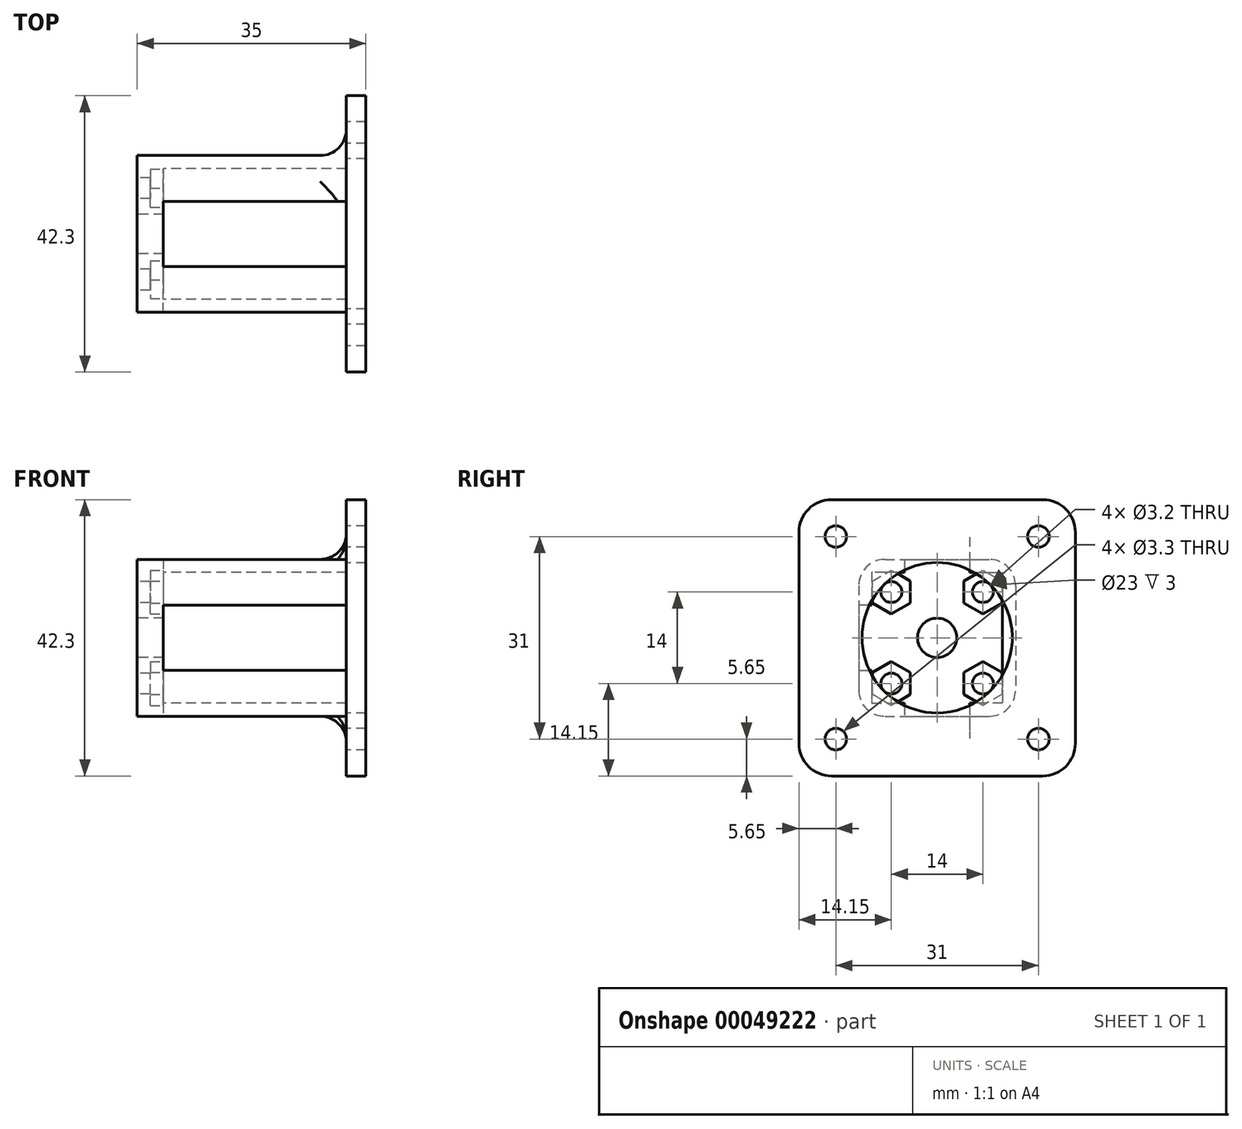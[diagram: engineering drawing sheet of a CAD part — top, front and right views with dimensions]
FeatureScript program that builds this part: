
annotation { "Feature Type Name" : "Feature", "Feature Type Description" : "" }
export const myFeature = defineFeature(function(context is Context, id is Id, definition is map)
    precondition{}
    {
        {
            var Q0;
            Q0=qCreatedBy(makeId("Right.planeOp"),FACE);
            var sketch = newSketch(context, id + "F0", { "sketchPlane" : qUnion([Q0])});
            skCircle(sketch, "E0", {"center": v(-15.5, 15.5) * mm, "radius": 1.65 * mm});
            skCircle(sketch, "E1", {"center": v(-15.5, -15.5) * mm, "radius": 1.65 * mm});
            skCircle(sketch, "E2", {"center": v(15.5, -15.5) * mm, "radius": 1.65 * mm});
            skCircle(sketch, "E3", {"center": v(15.5, 15.5) * mm, "radius": 1.65 * mm});
            skLineSegment(sketch, "E4", {"start": v(0, 0) * mm, "end": v(-15.5, 15.5) * mm, "construction": true});
            skLineSegment(sketch, "E5", {"start": v(0, 0) * mm, "end": v(15.5, -15.5) * mm, "construction": true});
            skLineSegment(sketch, "E6", {"start": v(15.5, 15.5) * mm, "end": v(0, 0) * mm, "construction": true});
            skLineSegment(sketch, "E7", {"start": v(0, 0) * mm, "end": v(-15.5, -15.5) * mm, "construction": true});
            skLineSegment(sketch, "E8.bottom", {"start": v(-21.15, 21.15) * mm, "end": v(21.15, 21.15) * mm, "construction": true});
            skLineSegment(sketch, "E8.top", {"start": v(-21.15, -21.15) * mm, "end": v(21.15, -21.15) * mm, "construction": true});
            skLineSegment(sketch, "E8.left", {"start": v(-21.15, 21.15) * mm, "end": v(-21.15, -21.15) * mm, "construction": true});
            skLineSegment(sketch, "E8.right", {"start": v(21.15, 21.15) * mm, "end": v(21.15, -21.15) * mm, "construction": true});
            skPoint(sketch, "E8.middle", {"position": v(0, 0) * mm});
            skCircle(sketch, "E9", {"center": v(-7, 7) * mm, "radius": 1.6 * mm});
            skCircle(sketch, "E10", {"center": v(-7, -7) * mm, "radius": 1.6 * mm});
            skCircle(sketch, "E11", {"center": v(7, -7) * mm, "radius": 1.6 * mm});
            skCircle(sketch, "E12", {"center": v(7, 7) * mm, "radius": 1.6 * mm});
            skLineSegment(sketch, "E13", {"start": v(-7, 7) * mm, "end": v(7, -7) * mm, "construction": true});
            skLineSegment(sketch, "E14", {"start": v(7, 7) * mm, "end": v(-7, -7) * mm, "construction": true});
            skLineSegment(sketch, "E15.bottom", {"start": v(-7, 7) * mm, "end": v(7, 7) * mm, "construction": true});
            skLineSegment(sketch, "E15.top", {"start": v(-7, -7) * mm, "end": v(7, -7) * mm, "construction": true});
            skLineSegment(sketch, "E15.left", {"start": v(-7, 7) * mm, "end": v(-7, -7) * mm, "construction": true});
            skLineSegment(sketch, "E15.right", {"start": v(7, 7) * mm, "end": v(7, -7) * mm, "construction": true});
            skLineSegment(sketch, "E16.bottom", {"start": v(-12, 12) * mm, "end": v(12, 12) * mm});
            skLineSegment(sketch, "E16.top", {"start": v(-12, -12) * mm, "end": v(12, -12) * mm});
            skLineSegment(sketch, "E16.left", {"start": v(-12, 12) * mm, "end": v(-12, -12) * mm});
            skLineSegment(sketch, "E16.right", {"start": v(12, 12) * mm, "end": v(12, -12) * mm});
            skCircle(sketch, "E17", {"center": v(0, 0) * mm, "radius": 3 * mm});
            skSolve(sketch);
        }
        {
            var Q0;
            Q0=makeQuery(id+"F0.imprint","IMPRINT",FACE,{"disambiguationData":[TD([[makeQuery(id+"F0.imprint","IMPRINT",EDGE,{"derivedFrom":sQuery(id+"F0.wireOp",EDGE,"E9")}),-1.0]])]});
            extrude(context, id + "F1", {"entities" : qUnion([Q0]), "depth" : 4 * mm, "offsetDistance" : 25 * mm});
        }
        {
            var Q0;
            Q0=makeQuery(id+"F1.opExtrude","CAP_FACE",FACE,{"disambiguationData":[OSD([sQuery(id+"F0.wireOp",EDGE,"E9"),sQuery(id+"F0.wireOp",EDGE,"E10"),sQuery(id+"F0.wireOp",EDGE,"E11"),sQuery(id+"F0.wireOp",EDGE,"E12"),sQuery(id+"F0.wireOp",EDGE,"E16.bottom"),sQuery(id+"F0.wireOp",EDGE,"E16.top"),sQuery(id+"F0.wireOp",EDGE,"E16.left"),sQuery(id+"F0.wireOp",EDGE,"E16.right"),sQuery(id+"F0.wireOp",EDGE,"E17")])],"isStart":false});
            var sketch = newSketch(context, id + "F2", { "sketchPlane" : qUnion([Q0])});
            skCircle(sketch, "E18.cCircle", {"center": v(7, -7) * mm, "radius": 2.9 * mm, "construction": true});
            skLineSegment(sketch, "E18.0", {"start": v(4.1, -5.33) * mm, "end": v(7, -3.65) * mm});
            skLineSegment(sketch, "E18.1", {"start": v(7, -3.65) * mm, "end": v(9.9, -5.33) * mm});
            skLineSegment(sketch, "E18.2", {"start": v(9.9, -5.33) * mm, "end": v(9.9, -8.67) * mm});
            skLineSegment(sketch, "E18.3", {"start": v(9.9, -8.67) * mm, "end": v(7, -10.35) * mm});
            skLineSegment(sketch, "E18.4", {"start": v(7, -10.35) * mm, "end": v(4.1, -8.67) * mm});
            skLineSegment(sketch, "E18.5", {"start": v(4.1, -8.67) * mm, "end": v(4.1, -5.33) * mm});
            skPoint(sketch, "E18.0.midPoint", {"position": v(5.55, -4.49) * mm});
            skCircle(sketch, "E19.cCircle", {"center": v(7, 7) * mm, "radius": 2.9 * mm, "construction": true});
            skLineSegment(sketch, "E19.0", {"start": v(7, 3.65) * mm, "end": v(4.1, 5.33) * mm});
            skLineSegment(sketch, "E19.1", {"start": v(4.1, 5.33) * mm, "end": v(4.1, 8.67) * mm});
            skLineSegment(sketch, "E19.2", {"start": v(4.1, 8.67) * mm, "end": v(7, 10.35) * mm});
            skLineSegment(sketch, "E19.3", {"start": v(7, 10.35) * mm, "end": v(9.9, 8.67) * mm});
            skLineSegment(sketch, "E19.4", {"start": v(9.9, 8.67) * mm, "end": v(9.9, 5.33) * mm});
            skLineSegment(sketch, "E19.5", {"start": v(9.9, 5.33) * mm, "end": v(7, 3.65) * mm});
            skPoint(sketch, "E19.0.midPoint", {"position": v(5.55, 4.49) * mm});
            skCircle(sketch, "E20.cCircle", {"center": v(-7, 7) * mm, "radius": 2.9 * mm, "construction": true});
            skLineSegment(sketch, "E20.0", {"start": v(-7, 3.65) * mm, "end": v(-9.9, 5.33) * mm});
            skLineSegment(sketch, "E20.1", {"start": v(-9.9, 5.33) * mm, "end": v(-9.9, 8.67) * mm});
            skLineSegment(sketch, "E20.2", {"start": v(-9.9, 8.67) * mm, "end": v(-7, 10.35) * mm});
            skLineSegment(sketch, "E20.3", {"start": v(-7, 10.35) * mm, "end": v(-4.1, 8.67) * mm});
            skLineSegment(sketch, "E20.4", {"start": v(-4.1, 8.67) * mm, "end": v(-4.1, 5.33) * mm});
            skLineSegment(sketch, "E20.5", {"start": v(-4.1, 5.33) * mm, "end": v(-7, 3.65) * mm});
            skPoint(sketch, "E20.0.midPoint", {"position": v(-8.45, 4.49) * mm});
            skCircle(sketch, "E21.cCircle", {"center": v(-7, -7) * mm, "radius": 2.9 * mm, "construction": true});
            skLineSegment(sketch, "E21.0", {"start": v(-7, -3.65) * mm, "end": v(-4.1, -5.33) * mm});
            skLineSegment(sketch, "E21.1", {"start": v(-4.1, -5.33) * mm, "end": v(-4.1, -8.67) * mm});
            skLineSegment(sketch, "E21.2", {"start": v(-4.1, -8.67) * mm, "end": v(-7, -10.35) * mm});
            skLineSegment(sketch, "E21.3", {"start": v(-7, -10.35) * mm, "end": v(-9.9, -8.67) * mm});
            skLineSegment(sketch, "E21.4", {"start": v(-9.9, -8.67) * mm, "end": v(-9.9, -5.33) * mm});
            skLineSegment(sketch, "E21.5", {"start": v(-9.9, -5.33) * mm, "end": v(-7, -3.65) * mm});
            skPoint(sketch, "E21.0.midPoint", {"position": v(-5.55, -4.49) * mm});
            skSolve(sketch);
        }
        {
            var Q0;
            Q0=makeQuery(id+"F1.opExtrude","CAP_FACE",FACE,{"disambiguationData":[OSD([sQuery(id+"F0.wireOp",EDGE,"E9"),sQuery(id+"F0.wireOp",EDGE,"E10"),sQuery(id+"F0.wireOp",EDGE,"E11"),sQuery(id+"F0.wireOp",EDGE,"E12"),sQuery(id+"F0.wireOp",EDGE,"E16.bottom"),sQuery(id+"F0.wireOp",EDGE,"E16.top"),sQuery(id+"F0.wireOp",EDGE,"E16.left"),sQuery(id+"F0.wireOp",EDGE,"E16.right"),sQuery(id+"F0.wireOp",EDGE,"E17")])],"isStart":false});
            var sketch = newSketch(context, id + "F3", { "sketchPlane" : qUnion([Q0])});
            skLineSegment(sketch, "E22.bottom", {"start": v(-12, 12) * mm, "end": v(12, 12) * mm});
            skLineSegment(sketch, "E22.top", {"start": v(-12, -12) * mm, "end": v(12, -12) * mm});
            skLineSegment(sketch, "E22.left", {"start": v(-12, 12) * mm, "end": v(-12, -12) * mm});
            skLineSegment(sketch, "E22.right", {"start": v(12, 12) * mm, "end": v(12, -12) * mm});
            skLineSegment(sketch, "E23", {"start": v(-10, 10) * mm, "end": v(-10, 5) * mm});
            skLineSegment(sketch, "E24", {"start": v(-10, 5) * mm, "end": v(-12, 5) * mm});
            skLineSegment(sketch, "E25", {"start": v(-12, 5) * mm, "end": v(-12, 12) * mm});
            skLineSegment(sketch, "E26", {"start": v(-5, 12) * mm, "end": v(-5, 10) * mm});
            skLineSegment(sketch, "E27", {"start": v(-5, 10) * mm, "end": v(-10, 10) * mm});
            skLineSegment(sketch, "E28", {"start": v(-10, -5) * mm, "end": v(-10, -10) * mm});
            skLineSegment(sketch, "E29", {"start": v(-10, -10) * mm, "end": v(-5, -10) * mm});
            skLineSegment(sketch, "E30", {"start": v(-5, -10) * mm, "end": v(-5, -12) * mm});
            skLineSegment(sketch, "E31", {"start": v(-5, -12) * mm, "end": v(-12, -12) * mm});
            skLineSegment(sketch, "E32", {"start": v(-12, -12) * mm, "end": v(-12, -5) * mm});
            skLineSegment(sketch, "E33", {"start": v(-12, -5) * mm, "end": v(-10, -5) * mm});
            skLineSegment(sketch, "E34", {"start": v(5, 12) * mm, "end": v(5, 10) * mm});
            skLineSegment(sketch, "E35", {"start": v(5, 10) * mm, "end": v(10, 10) * mm});
            skLineSegment(sketch, "E36", {"start": v(10, 10) * mm, "end": v(10, -10) * mm});
            skLineSegment(sketch, "E37", {"start": v(10, -10) * mm, "end": v(5, -10) * mm});
            skLineSegment(sketch, "E38", {"start": v(5, -10) * mm, "end": v(5, -12) * mm});
            skLineSegment(sketch, "E39", {"start": v(5, -12) * mm, "end": v(12, -12) * mm});
            skLineSegment(sketch, "E40", {"start": v(5, 12) * mm, "end": v(12, 12) * mm});
            skLineSegment(sketch, "E41", {"start": v(12, -12) * mm, "end": v(5, -12) * mm});
            skSolve(sketch);
        }
        {
            var Q0;
            Q0 = qSketchRegion(id + "F2", true);
            extrude(context, id + "F4", {"entities" : qUnion([Q0]), "operationType" : NewBodyOperationType.REMOVE, "oppositeDirection" : true, "depth" : 2 * mm, "offsetDistance" : 25 * mm});
        }
        {
            var Q0;
            Q0=makeQuery(id+"F3.imprint","IMPRINT",FACE,{"disambiguationData":[TD([[makeQuery(id+"F3.imprint","IMPRINT",EDGE,{"derivedFrom":sQuery(id+"F3.wireOp",EDGE,"E23")}),-1.0]])]});
            var Q1;
            Q1=makeQuery(id+"F3.imprint","IMPRINT",FACE,{"disambiguationData":[TD([[makeQuery(id+"F3.imprint","IMPRINT",EDGE,{"derivedFrom":sQuery(id+"F3.wireOp",EDGE,"E34")}),1.0]])]});
            var Q2;
            Q2=makeQuery(id+"F3.imprint","IMPRINT",FACE,{"disambiguationData":[TD([[makeQuery(id+"F3.imprint","IMPRINT",EDGE,{"derivedFrom":sQuery(id+"F3.wireOp",EDGE,"E28")}),-1.0]])]});
            extrude(context, id + "F5", {"entities" : qUnion([Q0, Q1, Q2]), "operationType" : NewBodyOperationType.ADD, "depth" : 28 * mm, "offsetDistance" : 25 * mm});
        }
        {
            var Q0;
            Q0=makeQuery(id+"F5.opExtrude","CAP_FACE",FACE,{"disambiguationData":[OSD([sQuery(id+"F3.wireOp",EDGE,"E22.bottom"),sQuery(id+"F3.wireOp",EDGE,"E23"),sQuery(id+"F3.wireOp",EDGE,"E24"),sQuery(id+"F3.wireOp",EDGE,"E25"),sQuery(id+"F3.wireOp",EDGE,"E26"),sQuery(id+"F3.wireOp",EDGE,"E27")])],"isStart":false});
            var sketch = newSketch(context, id + "F6", { "sketchPlane" : qUnion([Q0])});
            skCircle(sketch, "E42", {"center": v(-15.5, 15.5) * mm, "radius": 1.65 * mm});
            skCircle(sketch, "E43", {"center": v(-15.5, -15.5) * mm, "radius": 1.65 * mm});
            skCircle(sketch, "E44", {"center": v(15.5, -15.5) * mm, "radius": 1.65 * mm});
            skCircle(sketch, "E45", {"center": v(15.5, 15.5) * mm, "radius": 1.65 * mm});
            skLineSegment(sketch, "E46", {"start": v(0, 0) * mm, "end": v(-15.5, 15.5) * mm, "construction": true});
            skLineSegment(sketch, "E47", {"start": v(0, 0) * mm, "end": v(15.5, -15.5) * mm, "construction": true});
            skLineSegment(sketch, "E48", {"start": v(15.5, 15.5) * mm, "end": v(0, 0) * mm, "construction": true});
            skLineSegment(sketch, "E49", {"start": v(0, 0) * mm, "end": v(-15.5, -15.5) * mm, "construction": true});
            skLineSegment(sketch, "E50.bottom", {"start": v(-21.15, 21.15) * mm, "end": v(21.15, 21.15) * mm});
            skLineSegment(sketch, "E50.top", {"start": v(-21.15, -21.15) * mm, "end": v(21.15, -21.15) * mm});
            skLineSegment(sketch, "E50.left", {"start": v(-21.15, 21.15) * mm, "end": v(-21.15, -21.15) * mm});
            skLineSegment(sketch, "E50.right", {"start": v(21.15, 21.15) * mm, "end": v(21.15, -21.15) * mm});
            skPoint(sketch, "E50.middle", {"position": v(0, 0) * mm});
            skCircle(sketch, "E51", {"center": v(0, 0) * mm, "radius": 11.5 * mm});
            skSolve(sketch);
        }
        {
            var Q0;
            Q0 = qSketchRegion(id + "F6", true);
            extrude(context, id + "F7", {"entities" : qUnion([Q0]), "operationType" : NewBodyOperationType.ADD, "depth" : 3 * mm, "offsetDistance" : 25 * mm});
        }
        {
            var Q0;
            Q0=makeQuery(id+"F7.opExtrude","SWEPT_EDGE",EDGE,{"disambiguationData":[OSD([sQuery(id+"F6.wireOp",EDGE,"E50.bottom"),sQuery(id+"F6.wireOp",EDGE,"E50.right")])]});
            var Q1;
            Q1=makeQuery(id+"F7.opExtrude","SWEPT_EDGE",EDGE,{"disambiguationData":[OSD([sQuery(id+"F6.wireOp",EDGE,"E50.top"),sQuery(id+"F6.wireOp",EDGE,"E50.right")])]});
            var Q2;
            Q2=makeQuery(id+"F7.opExtrude","SWEPT_EDGE",EDGE,{"disambiguationData":[OSD([sQuery(id+"F6.wireOp",EDGE,"E50.top"),sQuery(id+"F6.wireOp",EDGE,"E50.left")])]});
            var Q3;
            Q3=makeQuery(id+"F7.opExtrude","SWEPT_EDGE",EDGE,{"disambiguationData":[OSD([sQuery(id+"F6.wireOp",EDGE,"E50.bottom"),sQuery(id+"F6.wireOp",EDGE,"E50.left")])]});
            fillet(context, id + "F8", {"entities" : qUnion([Q0, Q1, Q2, Q3]), "radius" : 5 * mm, "tangentPropagation" : true, "allowEdgeOverflow" : false});
        }
        {
            var Q0;
            Q0=makeQuery(id+"F5.boolean.opBoolean","MERGE",EDGE,{"derivedFrom":[makeQuery(id+"F1.opExtrude","SWEPT_EDGE",EDGE,{"disambiguationData":[OSD([sQuery(id+"F0.wireOp",EDGE,"E16.bottom"),sQuery(id+"F0.wireOp",EDGE,"E16.right")])]}),makeQuery(id+"F5.opExtrude","SWEPT_EDGE",EDGE,{"disambiguationData":[OSD([sQuery(id+"F3.wireOp",EDGE,"E22.right"),sQuery(id+"F3.wireOp",EDGE,"E40")])]})]});
            var Q1;
            Q1=makeQuery(id+"F5.boolean.opBoolean","MERGE",EDGE,{"derivedFrom":[makeQuery(id+"F1.opExtrude","SWEPT_EDGE",EDGE,{"disambiguationData":[OSD([sQuery(id+"F0.wireOp",EDGE,"E16.top"),sQuery(id+"F0.wireOp",EDGE,"E16.right")])]}),makeQuery(id+"F5.opExtrude","SWEPT_EDGE",EDGE,{"disambiguationData":[OSD([sQuery(id+"F3.wireOp",EDGE,"E22.right"),sQuery(id+"F3.wireOp",EDGE,"E41")])]})]});
            var Q2;
            Q2=makeQuery(id+"F5.boolean.opBoolean","MERGE",EDGE,{"derivedFrom":[makeQuery(id+"F1.opExtrude","SWEPT_EDGE",EDGE,{"disambiguationData":[OSD([sQuery(id+"F0.wireOp",EDGE,"E16.top"),sQuery(id+"F0.wireOp",EDGE,"E16.left")])]}),makeQuery(id+"F5.opExtrude","SWEPT_EDGE",EDGE,{"disambiguationData":[OSD([sQuery(id+"F3.wireOp",EDGE,"E31"),sQuery(id+"F3.wireOp",EDGE,"E32")])]})]});
            var Q3;
            Q3=makeQuery(id+"F5.boolean.opBoolean","MERGE",EDGE,{"derivedFrom":[makeQuery(id+"F1.opExtrude","SWEPT_EDGE",EDGE,{"disambiguationData":[OSD([sQuery(id+"F0.wireOp",EDGE,"E16.bottom"),sQuery(id+"F0.wireOp",EDGE,"E16.left")])]}),makeQuery(id+"F5.opExtrude","SWEPT_EDGE",EDGE,{"disambiguationData":[OSD([sQuery(id+"F3.wireOp",EDGE,"E22.bottom"),sQuery(id+"F3.wireOp",EDGE,"E25")])]})]});
            var Q4;
            Q4=makeQuery(id+"F5.opExtrude","CAP_EDGE",EDGE,{"disambiguationData":[OSD([sQuery(id+"F3.wireOp",EDGE,"E22.right")])],"isStart":false});
            var Q5;
            Q5=makeQuery(id+"F5.opExtrude","CAP_EDGE",EDGE,{"disambiguationData":[OSD([sQuery(id+"F3.wireOp",EDGE,"E31")])],"isStart":false});
            var Q6;
            Q6=makeQuery(id+"F5.opExtrude","CAP_EDGE",EDGE,{"disambiguationData":[OSD([sQuery(id+"F3.wireOp",EDGE,"E25")])],"isStart":false});
            fillet(context, id + "F9", {"entities" : qUnion([Q0, Q1, Q2, Q3, Q4, Q5, Q6]), "radius" : 4 * mm, "tangentPropagation" : true, "allowEdgeOverflow" : false});
        }
    });
